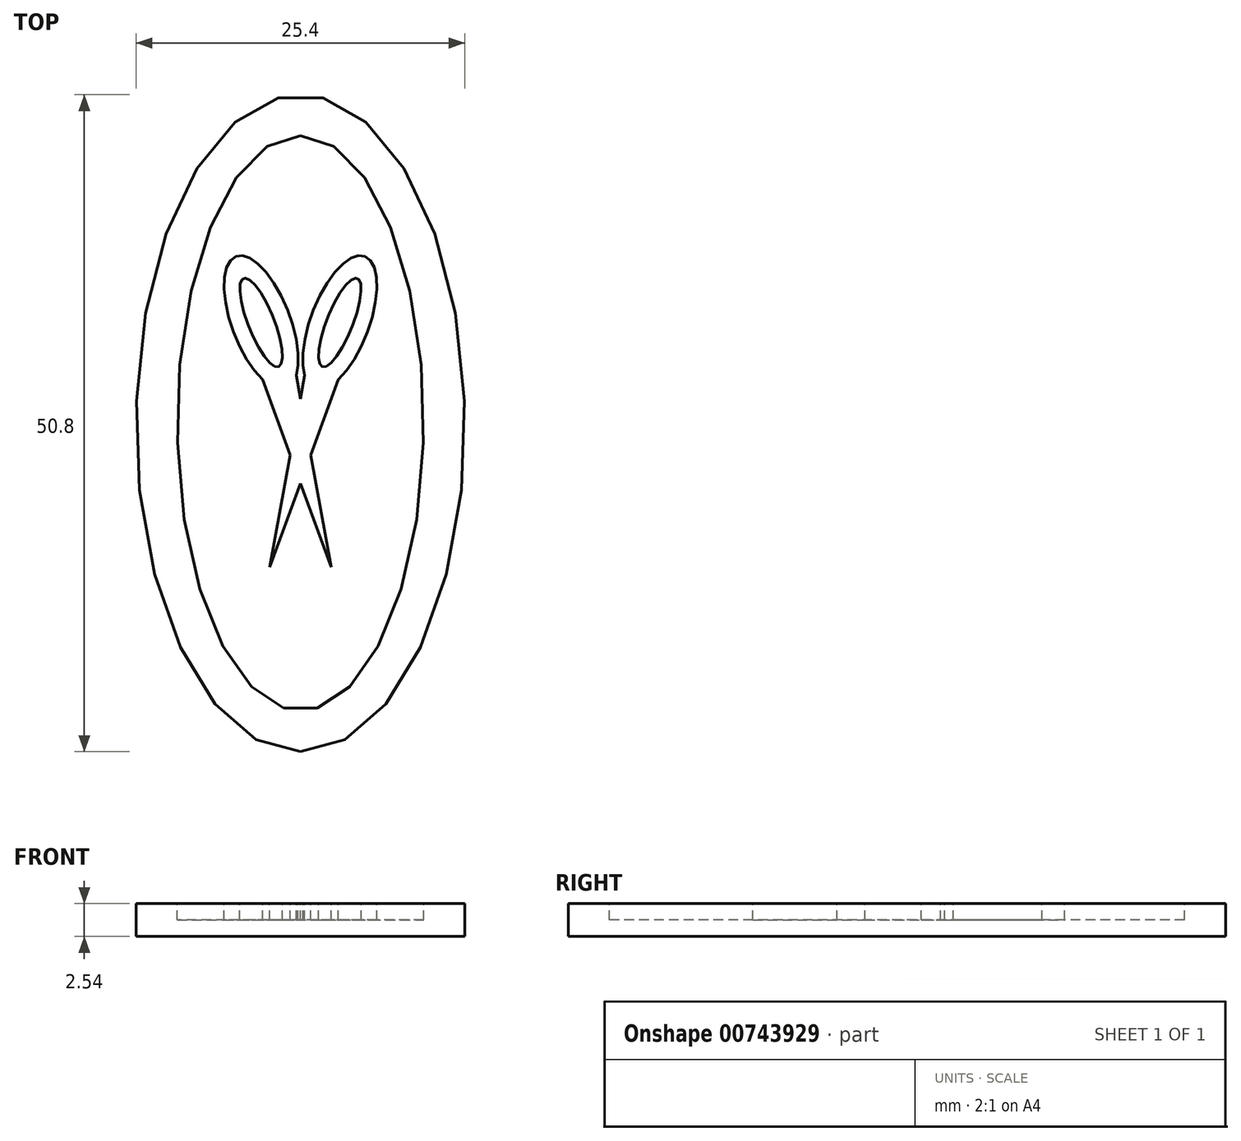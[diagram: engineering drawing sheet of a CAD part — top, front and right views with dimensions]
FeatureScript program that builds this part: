
annotation { "Feature Type Name" : "Feature", "Feature Type Description" : "" }
export const myFeature = defineFeature(function(context is Context, id is Id, definition is map)
    precondition{}
    {
        {
            var Q0;
            Q0=qCreatedBy(makeId("Top.planeOp"),FACE);
            var sketch = newSketch(context, id + "F0", { "sketchPlane" : qUnion([Q0])});
            skEllipse(sketch, "E0", {"center": v(0, 0) * mm, "majorRadius": 25.4 * mm, "minorRadius": 12.7 * mm, "majorAxis": v(0, -1)});
            skSolve(sketch);
        }
        {
            var Q0;
            Q0=qSketchRegion(id+"F0",true);
            extrude(context, id + "F1", {"entities" : qUnion([Q0]), "depth" : 2.54 * mm, "offsetDistance" : 25.4 * mm});
        }
        {
            var Q0;
            Q0=makeQuery(id+"F1.opExtrude","CAP_FACE",FACE,{"disambiguationData":[OSD([sQuery(id+"F0.wireOp",EDGE,"E0")])],"isStart":false});
            var sketch = newSketch(context, id + "F2", { "sketchPlane" : qUnion([Q0])});
            skEllipse(sketch, "E1", {"center": v(0, 0) * mm, "majorRadius": 22.23 * mm, "minorRadius": 9.53 * mm, "majorAxis": v(0, 1)});
            skSolve(sketch);
        }
        {
            var Q0;
            Q0=qSketchRegion(id+"F2",true);
            extrude(context, id + "F3", {"entities" : qUnion([Q0]), "operationType" : NewBodyOperationType.REMOVE, "oppositeDirection" : true, "depth" : 1.27 * mm, "offsetDistance" : 25.4 * mm});
        }
        {
            var Q0;
            Q0=makeQuery(id+"F2.imprint","IMPRINT",FACE,{"disambiguationData":[TD([[makeQuery(id+"F2.imprint","IMPRINT",EDGE,{"derivedFrom":sQuery(id+"F2.wireOp",EDGE,"E1")}),1.0]])]});
            var sketch = newSketch(context, id + "F4", { "sketchPlane" : qUnion([Q0])});
            skEllipse(sketch, "E2", {"center": v(3.04, 7.79) * mm, "majorRadius": 5.47 * mm, "minorRadius": 2.26 * mm, "majorAxis": v(-0.35, -0.94)});
            skEllipse(sketch, "E3", {"center": v(3.04, 7.79) * mm, "majorRadius": 3.67 * mm, "minorRadius": 1 * mm, "majorAxis": v(-0.37, -0.93)});
            skLineSegment(sketch, "E4", {"start": v(-2.37, -11.14) * mm, "end": v(2.93, 3.37) * mm});
            skLineSegment(sketch, "E5", {"start": v(-2.37, -11.14) * mm, "end": v(0.33, 3.68) * mm});
            skLineSegment(sketch, "E6.0", {"start": v(-6.94, 8.53) * mm, "end": v(-6.2, 14.16) * mm, "construction": true});
            skEllipse(sketch, "E7.MirrorC", {"center": v(-3.04, 7.79) * mm, "majorRadius": 5.47 * mm, "minorRadius": 2.26 * mm, "majorAxis": v(0.35, -0.94)});
            skEllipse(sketch, "E8.MirrorC", {"center": v(-3.04, 7.79) * mm, "majorRadius": 3.67 * mm, "minorRadius": 1 * mm, "majorAxis": v(0.37, -0.93)});
            skLineSegment(sketch, "E9.MirrorCS", {"start": v(2.37, -11.14) * mm, "end": v(-0.33, 3.68) * mm});
            skLineSegment(sketch, "E10.MirrorCS", {"start": v(2.37, -11.14) * mm, "end": v(-2.93, 3.37) * mm});
            skSolve(sketch);
        }
        {
            var Q0;
            Q0=qSketchRegion(id+"F4",true);
            extrude(context, id + "F5", {"entities" : qUnion([Q0]), "operationType" : NewBodyOperationType.ADD, "oppositeDirection" : true, "depth" : 1.52 * mm, "offsetDistance" : 25.4 * mm});
        }
    });
